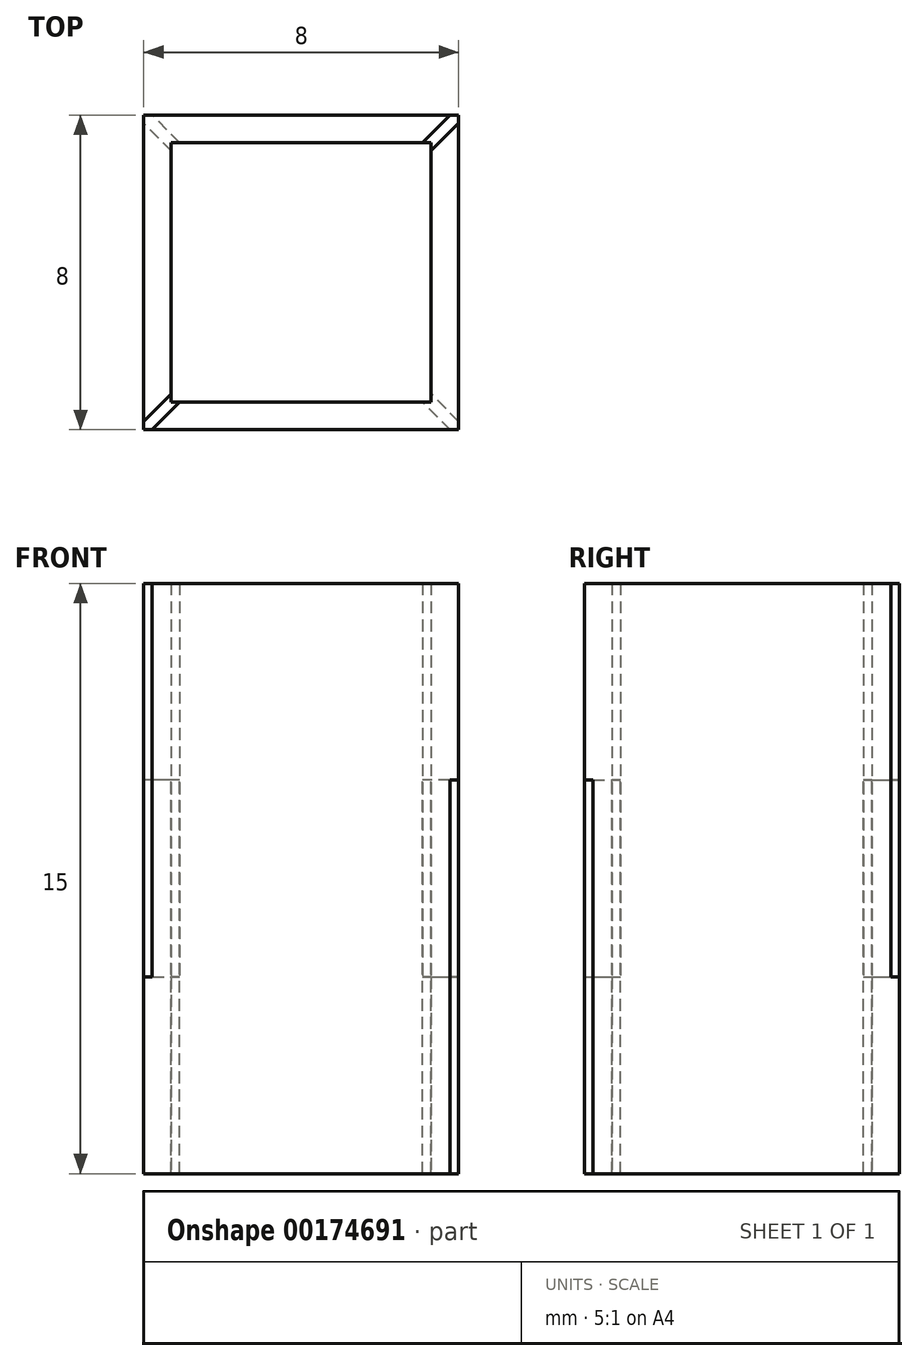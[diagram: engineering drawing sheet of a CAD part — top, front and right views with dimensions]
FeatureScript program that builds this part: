
annotation { "Feature Type Name" : "Feature", "Feature Type Description" : "" }
export const myFeature = defineFeature(function(context is Context, id is Id, definition is map)
    precondition{}
    {
        {
            var Q0;
            Q0=qCreatedBy(makeId("Top.planeOp"),FACE);
            var sketch = newSketch(context, id + "F0", { "sketchPlane" : qUnion([Q0])});
            skLineSegment(sketch, "E0.bottom", {"start": v(4, -4) * mm, "end": v(-4, -4) * mm});
            skLineSegment(sketch, "E0.top", {"start": v(4, 4) * mm, "end": v(-4, 4) * mm});
            skLineSegment(sketch, "E0.left", {"start": v(4, -4) * mm, "end": v(4, 4) * mm});
            skLineSegment(sketch, "E0.right", {"start": v(-4, -4) * mm, "end": v(-4, 4) * mm});
            skPoint(sketch, "E0.middle", {"position": v(0, 0) * mm});
            skLineSegment(sketch, "E1.bottom", {"start": v(3.3, -3.3) * mm, "end": v(-3.3, -3.3) * mm});
            skLineSegment(sketch, "E1.top", {"start": v(3.3, 3.3) * mm, "end": v(-3.3, 3.3) * mm});
            skLineSegment(sketch, "E1.left", {"start": v(3.3, -3.3) * mm, "end": v(3.3, 3.3) * mm});
            skLineSegment(sketch, "E1.right", {"start": v(-3.3, -3.3) * mm, "end": v(-3.3, 3.3) * mm});
            skLineSegment(sketch, "E2", {"start": v(-4, -4) * mm, "end": v(-3.3, -3.3) * mm, "construction": true});
            skLineSegment(sketch, "E3.trimOffspring", {"start": v(3.3, 3.3) * mm, "end": v(4, 4) * mm, "construction": true});
            skLineSegment(sketch, "E4.0", {"start": v(-3.79, -4) * mm, "end": v(-3.09, -3.3) * mm});
            skLineSegment(sketch, "E5", {"start": v(-4, -3.79) * mm, "end": v(-3.3, -3.09) * mm});
            skLineSegment(sketch, "E6.trimOffspring", {"start": v(3.09, 3.3) * mm, "end": v(3.79, 4) * mm});
            skLineSegment(sketch, "E7.trimOffspring", {"start": v(3.3, 3.09) * mm, "end": v(4, 3.79) * mm});
            skSolve(sketch);
        }
        {
            var Q0;
            {var subQ3=sQuery(id+"F0.wireOp",EDGE,"E5");Q0=makeQuery(id+"F0.imprint","IMPRINT",FACE,{"disambiguationData":[TD([[makeQuery(id+"F0.imprint","IMPRINT",EDGE,{"derivedFrom":subQ3}),1.0]])]});}
            var Q1;
            {var subQ4=sQuery(id+"F0.wireOp",EDGE,"E4.0");Q1=makeQuery(id+"F0.imprint","IMPRINT",FACE,{"disambiguationData":[TD([[makeQuery(id+"F0.imprint","IMPRINT",EDGE,{"derivedFrom":subQ4}),-1.0]])]});}
            var Q2;
            Q2=sQuery(id+"F0.wireOp",EDGE,"E2");
            extrude(context, id + "F1", {"entities" : qUnion([Q0, Q1]), "surfaceEntities" : qUnion([Q2]), "depth" : 15 * mm});
        }
        {
            var Q0;
            {var subQ4=sQuery(id+"F0.wireOp",EDGE,"E4.0");Q0=makeQuery(id+"F0.imprint","IMPRINT",FACE,{"disambiguationData":[TD([[makeQuery(id+"F0.imprint","IMPRINT",EDGE,{"derivedFrom":subQ4}),1.0]])]});}
            var Q1;
            {var subQ4=sQuery(id+"F0.wireOp",EDGE,"E6.trimOffspring");Q1=makeQuery(id+"F0.imprint","IMPRINT",FACE,{"disambiguationData":[TD([[makeQuery(id+"F0.imprint","IMPRINT",EDGE,{"derivedFrom":subQ4}),-1.0]])]});}
            extrude(context, id + "F2", {"entities" : qUnion([Q0, Q1]), "operationType" : NewBodyOperationType.ADD, "depth" : 5 * mm});
        }
        {
            var Q0;
            Q0=makeQuery(id+"F1.opExtrude","SWEPT_BODY",BODY,{"disambiguationData":[OSD([sQuery(id+"F0.wireOp",EDGE,"E0.bottom"),sQuery(id+"F0.wireOp",EDGE,"E0.left"),sQuery(id+"F0.wireOp",EDGE,"E1.bottom"),sQuery(id+"F0.wireOp",EDGE,"E1.left"),sQuery(id+"F0.wireOp",EDGE,"E4.0"),sQuery(id+"F0.wireOp",EDGE,"E7.trimOffspring")])]});
            var Q1;
            Q1=makeQuery(id+"F1.opExtrude","CAP_FACE",FACE,{"disambiguationData":[OSD([sQuery(id+"F0.wireOp",EDGE,"E0.top"),sQuery(id+"F0.wireOp",EDGE,"E0.right"),sQuery(id+"F0.wireOp",EDGE,"E1.top"),sQuery(id+"F0.wireOp",EDGE,"E1.right"),sQuery(id+"F0.wireOp",EDGE,"E5"),sQuery(id+"F0.wireOp",EDGE,"E6.trimOffspring")])],"isStart":false});
            mirror(context, id + "F3", {"entities" : qUnion([Q0]), "mirrorPlane" : qUnion([Q1])});
        }
        {
            var Q0;
            Q0=makeQuery(id+"F3.opPattern","COPY",BODY,{"derivedFrom":makeQuery(id+"F1.opExtrude","SWEPT_BODY",BODY,{"disambiguationData":[OSD([sQuery(id+"F0.wireOp",EDGE,"E0.bottom"),sQuery(id+"F0.wireOp",EDGE,"E0.left"),sQuery(id+"F0.wireOp",EDGE,"E1.bottom"),sQuery(id+"F0.wireOp",EDGE,"E1.left"),sQuery(id+"F0.wireOp",EDGE,"E4.0"),sQuery(id+"F0.wireOp",EDGE,"E7.trimOffspring")])]}),"instanceName":"1"});
            var Q1;
            Q1=makeQuery(id+"F3.opPattern","COPY",EDGE,{"derivedFrom":makeQuery(id+"F1.opExtrude","SWEPT_EDGE",EDGE,{"disambiguationData":[OSD([sQuery(id+"F0.wireOp",EDGE,"E0.bottom"),sQuery(id+"F0.wireOp",EDGE,"E0.left")])]}),"instanceName":"1"});
            transform(context, id + "F4", {"entities" : qUnion([Q0]), "transformType" : TransformType.ROTATION, "transformAxis" : qUnion([Q1]), "angle" : 90 * degree, "makeCopy" : false});
        }
        {
            var Q0;
            Q0=makeQuery(id+"F3.opPattern","COPY",BODY,{"derivedFrom":makeQuery(id+"F1.opExtrude","SWEPT_BODY",BODY,{"disambiguationData":[OSD([sQuery(id+"F0.wireOp",EDGE,"E0.bottom"),sQuery(id+"F0.wireOp",EDGE,"E0.left"),sQuery(id+"F0.wireOp",EDGE,"E1.bottom"),sQuery(id+"F0.wireOp",EDGE,"E1.left"),sQuery(id+"F0.wireOp",EDGE,"E4.0"),sQuery(id+"F0.wireOp",EDGE,"E7.trimOffspring")])]}),"instanceName":"1"});
            var Q1;
            Q1=makeQuery(id+"F3.opPattern","COPY",VERTEX,{"derivedFrom":makeQuery(id+"F2.opExtrude","CAP_VERTEX",VERTEX,{"disambiguationData":[OSD([sQuery(id+"F0.wireOp",EDGE,"E0.bottom"),sQuery(id+"F0.wireOp",EDGE,"E0.right")])],"isStart":true}),"instanceName":"1"});
            var Q2;
            Q2=makeQuery(id+"F1.opExtrude","CAP_VERTEX",VERTEX,{"disambiguationData":[OSD([sQuery(id+"F0.wireOp",EDGE,"E0.bottom"),sQuery(id+"F0.wireOp",EDGE,"E0.left")])],"isStart":false});
            transform(context, id + "F5", {"entities" : qUnion([Q0]), "transformType" : TransformType.TRANSLATION_ENTITY, "oppositeDirectionEntity" : false, "transformLine" : qUnion([Q1, Q2]), "makeCopy" : false});
        }
        {
            var Q0;
            Q0=makeQuery(id+"F1.opExtrude","SWEPT_BODY",BODY,{"disambiguationData":[OSD([sQuery(id+"F0.wireOp",EDGE,"E0.bottom"),sQuery(id+"F0.wireOp",EDGE,"E0.left"),sQuery(id+"F0.wireOp",EDGE,"E1.bottom"),sQuery(id+"F0.wireOp",EDGE,"E1.left"),sQuery(id+"F0.wireOp",EDGE,"E4.0"),sQuery(id+"F0.wireOp",EDGE,"E7.trimOffspring")])]});
            var Q1;
            Q1=makeQuery(id+"F3.opPattern","COPY",BODY,{"derivedFrom":makeQuery(id+"F1.opExtrude","SWEPT_BODY",BODY,{"disambiguationData":[OSD([sQuery(id+"F0.wireOp",EDGE,"E0.bottom"),sQuery(id+"F0.wireOp",EDGE,"E0.left"),sQuery(id+"F0.wireOp",EDGE,"E1.bottom"),sQuery(id+"F0.wireOp",EDGE,"E1.left"),sQuery(id+"F0.wireOp",EDGE,"E4.0"),sQuery(id+"F0.wireOp",EDGE,"E7.trimOffspring")])]}),"instanceName":"1"});
            booleanBodies(context, id + "F6", {"operationType" : BooleanOperationType.INTERSECTION, "tools" : qUnion([Q0, Q1])});
        }
    });
